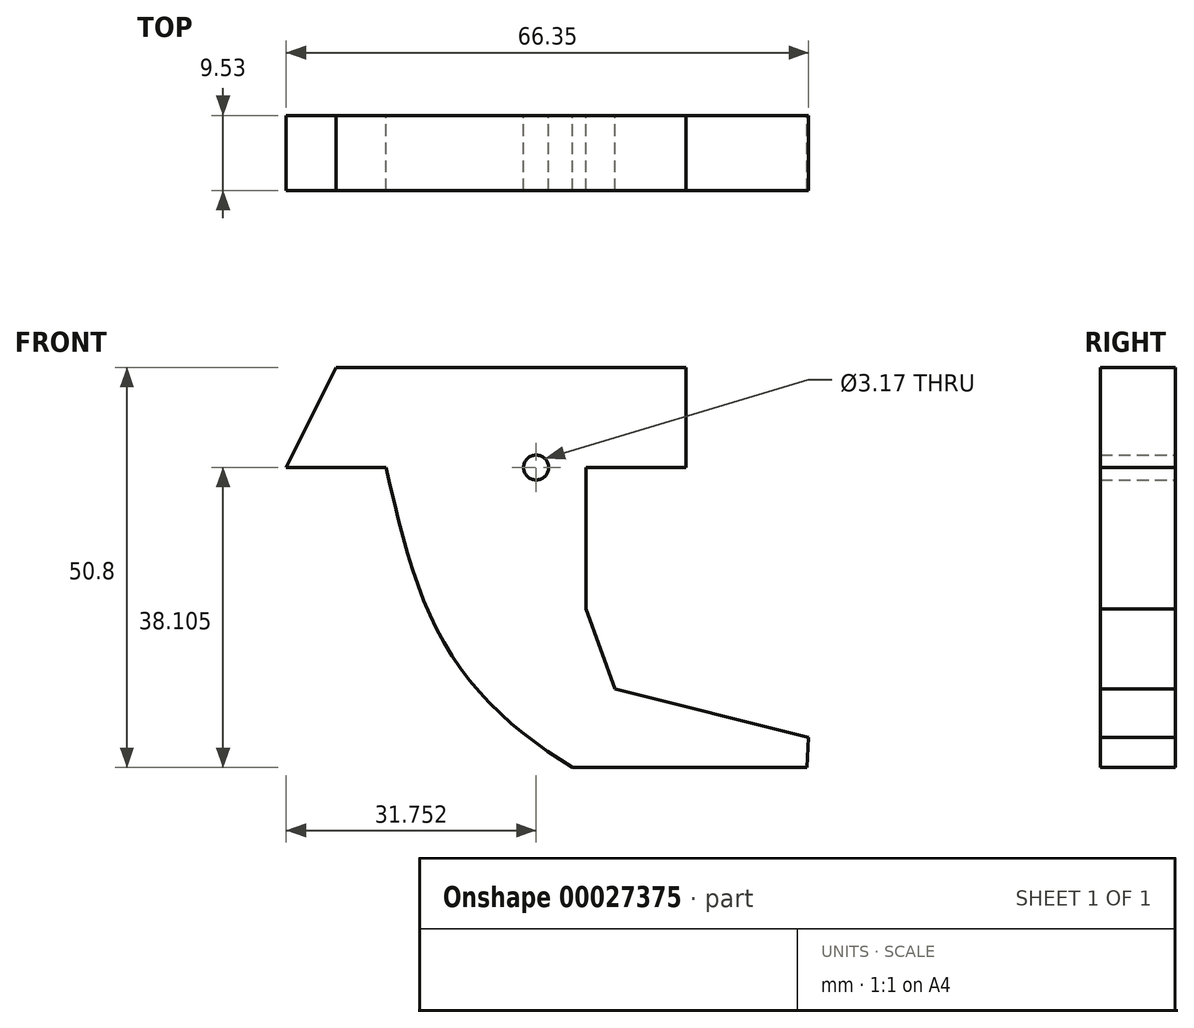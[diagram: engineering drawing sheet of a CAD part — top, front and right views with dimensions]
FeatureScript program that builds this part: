
annotation { "Feature Type Name" : "Feature", "Feature Type Description" : "" }
export const myFeature = defineFeature(function(context is Context, id is Id, definition is map)
    precondition{}
    {
        {
            var Q0;
            Q0=qCreatedBy(makeId("Front.planeOp"),FACE);
            var sketch = newSketch(context, id + "F0", { "sketchPlane" : qUnion([Q0])});
            skLineSegment(sketch, "E0.bottom", {"start": v(39.33, 30.68) * mm, "end": v(83.78, 30.68) * mm});
            skLineSegment(sketch, "E0.top", {"start": v(32.98, 17.98) * mm, "end": v(45.68, 17.98) * mm});
            skLineSegment(sketch, "E0.right", {"start": v(83.78, 30.68) * mm, "end": v(83.78, 17.98) * mm});
            skLineSegment(sketch, "E1", {"start": v(69.34, -20.12) * mm, "end": v(99.1, -20.12) * mm});
            skFitSpline(sketch, "E2", {"points": [v(45.68, 17.98) * mm, v(54.13, -6.1) * mm, v(69.34, -20.12) * mm], "startDerivative": vector(11.8, -52.96) * mm, "endDerivative": vector(36.92, -22.43) * mm});
            skLineSegment(sketch, "E3", {"start": v(71.08, 17.98) * mm, "end": v(71.08, 0) * mm});
            skLineSegment(sketch, "E4", {"start": v(71.08, 0) * mm, "end": v(74.72, -10.14) * mm});
            skLineSegment(sketch, "E5.trimOffspring", {"start": v(71.08, 17.98) * mm, "end": v(83.78, 17.98) * mm});
            skLineSegment(sketch, "E6", {"start": v(74.72, -10.14) * mm, "end": v(99.33, -16.27) * mm});
            skLineSegment(sketch, "E7", {"start": v(99.33, -16.27) * mm, "end": v(99.1, -20.12) * mm});
            skCircle(sketch, "E8", {"center": v(64.73, 17.98) * mm, "radius": 1.59 * mm});
            skLineSegment(sketch, "E9", {"start": v(32.98, 17.98) * mm, "end": v(39.33, 30.68) * mm});
            skPoint(sketch, "E0.left.start.orphan", {"position": v(32.98, 30.68) * mm});
            skLineSegment(sketch, "E10", {"start": v(32.98, 17.98) * mm, "end": v(32.98, 30.68) * mm});
            skSolve(sketch);
        }
        {
            var Q0;
            Q0=makeQuery(id+"F0.imprint","IMPRINT",FACE,{"disambiguationData":[TD([[makeQuery(id+"F0.imprint","IMPRINT",EDGE,{"derivedFrom":sQuery(id+"F0.wireOp",EDGE,"E0.bottom")}),-1.0]])]});
            extrude(context, id + "F1", {"entities" : qUnion([Q0]), "depth" : 9.52 * mm});
        }
    });
